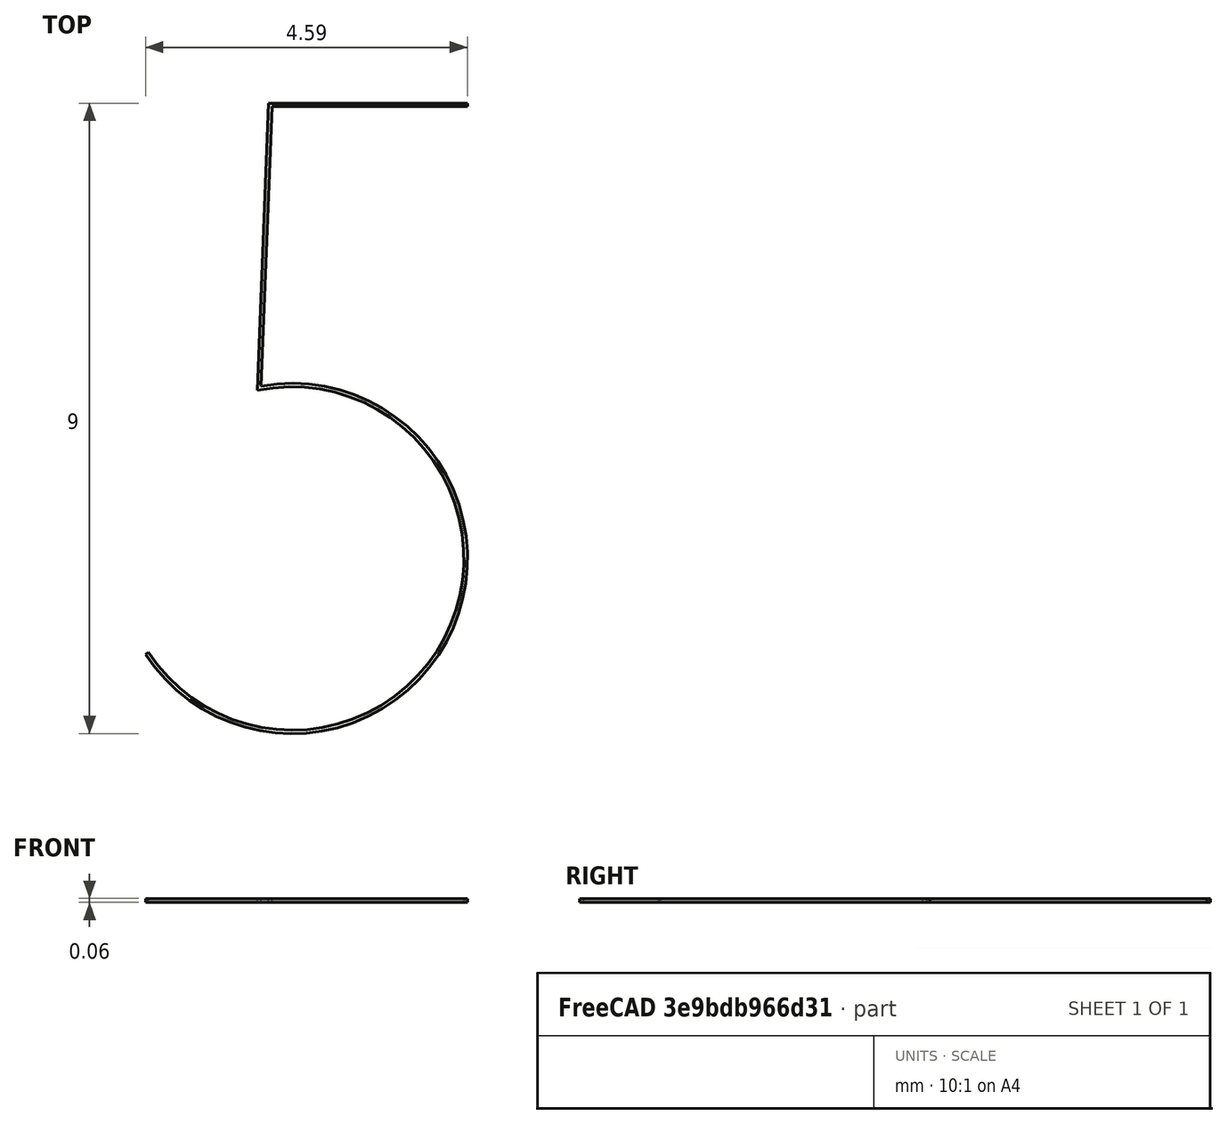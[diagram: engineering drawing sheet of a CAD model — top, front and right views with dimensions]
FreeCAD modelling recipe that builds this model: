
FCSTD DOCUMENT  (FreeCAD 0.16R6712 (Git))
Label: 5t
License: All rights reserved
LicenseURL: http://en.wikipedia.org/wiki/All_rights_reserved
objects: Sketcher::SketchObject×1, PartDesign::Pad×1, Mesh::Feature×1
note: 3 computed .brp shape members not serialized (recipe doc carries the construction recipe); baked Part::Feature solids carry a one-line shape summary decoded from their .brp

FEATURE [Sketcher::SketchObject] Sketch
  sketch-geometry (8):
    g0: ArcOfCircle CenterX=0 CenterY=2.5 CenterZ=0 NormalX=0 NormalY=0 NormalZ=1 Radius=2.5 StartAngle=3.72044 EndAngle=8.03284
    g1: LineSegment StartX=-0.444766 StartY=4.96012 StartZ=0 EndX=-0.285901 EndY=8.95 EndZ=0
    g2: LineSegment StartX=-0.285901 StartY=8.95 StartZ=0 EndX=2.5 EndY=8.95 EndZ=0
    g3: LineSegment StartX=-0.33395 StartY=9 StartZ=0 EndX=2.5 EndY=9 EndZ=0
    g4: LineSegment StartX=-0.33395 StartY=9 StartZ=0 EndX=-0.497239 EndY=4.89901 EndZ=0
    g5: ArcOfCircle CenterX=0 CenterY=2.5 CenterZ=0 NormalX=0 NormalY=0 NormalZ=1 Radius=2.45 StartAngle=3.72044 EndAngle=8.05836
    g6: LineSegment StartX=-2.05088 StartY=1.15971 StartZ=0 EndX=-2.09274 EndY=1.13235 EndZ=0
    g7: LineSegment StartX=2.5 StartY=8.95 StartZ=0 EndX=2.5 EndY=9 EndZ=0
  constraints (22):
    c: PointOnObject(g0,g-2)
    c: Coincident(g1,g0)
    c: Coincident(g2,g1)
    c: Horizontal(g2)
    c: Tangent(g0,g-1)
    c: Radius(g0) = 2.5
    c: Horizontal(g3)
    c: Coincident(g4,g3)
    c: Coincident(g5,g0)
    c: Coincident(g6,g5)
    c: Coincident(g6,g0)
    c: Perpendicular(g0,g6)
    c: Distance(g5,g0) = 0.05
    c: DistanceX(g-1,g2) = 2.5
    c: Coincident(g7,g3)
    c: Perpendicular(g7,g2)
    c: Coincident(g7,g2)
    c: DistanceY(g2,g3) = 0.05
    c: Distance(g-1,g3) = 9
    c: Parallel(g1,g4)
    c: Distance(g1,g4) = 0.05
    c: Coincident(g5,g4)
FEATURE [PartDesign::Pad] Pad
  Length = 0.05
  Length2 = 100
  Midplane = true
  Sketch = -> Sketch
  Type = 0
FEATURE [Mesh::Feature] Mesh  label="Pad (Meshed)"
